# Revit family: FP_Revit_18_HC90BHOBX1_Rangehood_90001853A
name_source: partatom
category: Specialty Equipment
revit_build: Autodesk Revit 2018 (Build: 20170223_1515(x64)
units: mm (PartAtom-declared; Revit-internal decimal feet)

## family parameters
Always vertical = Yes
Cut with Voids When Loaded = Yes
OmniClass Number = 23.40.40.00
OmniClass Title = Food Service Equipment and Furnishings
Part Type = Normal
Room Calculation Point = No
Round Connector Dimension = Use Diameter
Shared = No
Work Plane-Based = No

## types (1)
- FP_Revit_18_HC90BHOBX1_Rangehood_90001853A
    Chassis - Depth = 368 mm  [stored 1.20735 ft]
    Chassis - Height = 615 mm  [stored 2.01772 ft]
    Chassis - Width = 374 mm  [stored 1.22703 ft]
    Connector Description - Electrical = 220 V, 50 Hz, 158 W
    Connector Description - Extraction = 180mm Semi Rigid Rangehood Ducting, 1080m³/hr
    Description = 90cm Rangehood
    Manufacturer = Fisher & Paykel Appliances
    Material - Body = Fisher & Paykel - Stainless Steel
    Material - Glass = Fisher & Paykel - Black
    Model = HC90BHOBX1
    Product - Depth = 545 mm  [stored 1.78806 ft]
    Product - Width = 895 mm  [stored 2.93635 ft]
    URL = www.fisherpaykel.com

note: [stored X ft] marks values corroborated as IEEE doubles in the binary element streams (Revit-internal decimal feet)

## geometry (parser evidence)
native form markers: Sweep x5
no freeform markers — native parametric forms only
